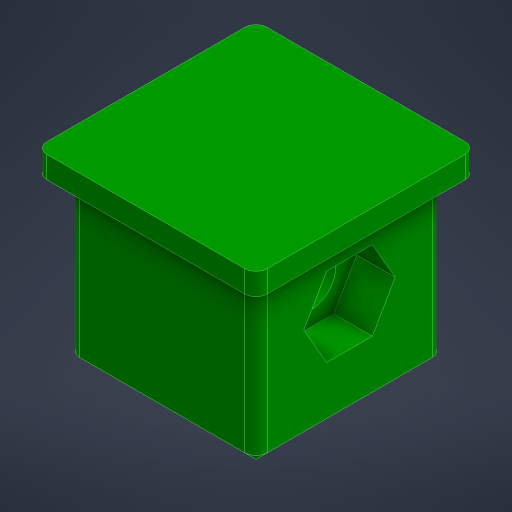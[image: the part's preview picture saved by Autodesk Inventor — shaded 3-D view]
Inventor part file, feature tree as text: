
AUTODESK INVENTOR PART (.ipt)
format: ipt  version: 2024 (Build 280153000, 153)  size: 253,440 bytes
history: native  units: mm
features: extrude x4, sketch x4, other x2, mirror x1, shell x1, fillet x1, chamfer x1
ambient origin geometry x8: Origin, YZ Plane, XZ Plane, XY Plane, X Axis, Y Axis, Z Axis, Center Point
bodies: Body1 (feature_tree)
feature tree (14):
  other  "Твердое тело1"
  extrude  "Выдавливание1"  Depth=17.0mm
  extrude  "Выдавливание2"  Depth=17.0mm
  other  "РабПлоскость1"
  mirror  "Зеркальное отражение1"
  shell  "Оболочка1"  Thickness=15.0mm
  extrude  "Выдавливание3"  Depth=7.2mm
  fillet  "Сопряжение1"  Radius=3.5mm
  chamfer  "Фаска1"  Distance=3.5mm
  extrude  "Выдавливание4"  Depth=20.0mm
  sketch  "Эскиз1"
  sketch  "Эскиз2"
  sketch  "Эскиз3"
  sketch  "Эскиз4"
